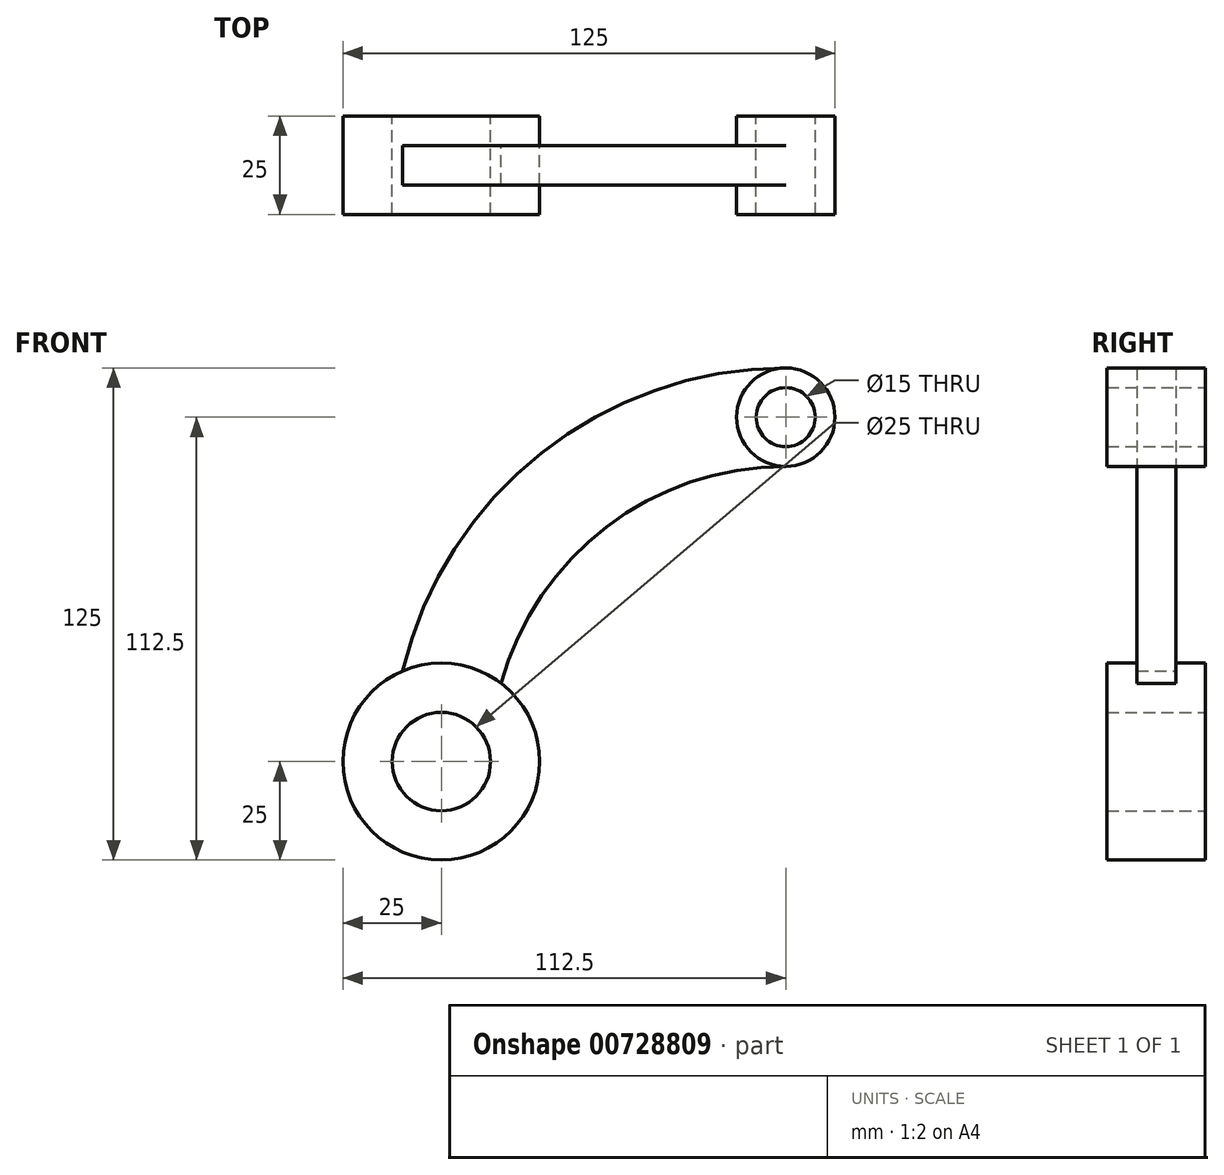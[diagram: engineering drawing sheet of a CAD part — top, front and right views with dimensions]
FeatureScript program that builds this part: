
annotation { "Feature Type Name" : "Feature", "Feature Type Description" : "" }
export const myFeature = defineFeature(function(context is Context, id is Id, definition is map)
    precondition{}
    {
        {
            var Q0;
            Q0=qCreatedBy(makeId("Front.planeOp"),FACE);
            var sketch = newSketch(context, id + "F0", { "sketchPlane" : qUnion([Q0])});
            skArc(sketch, "E0", {"start": v(0, 75) * mm, "mid": v(-45.47, 59.64) * mm, "end": v(-72.32, 19.86) * mm});
            skArc(sketch, "E1", {"start": v(0, 100) * mm, "mid": v(-62.05, 78.42) * mm, "end": v(-97.32, 22.99) * mm});
            skCircle(sketch, "E2", {"center": v(0, 87.5) * mm, "radius": 12.5 * mm});
            skCircle(sketch, "E3", {"center": v(0, 87.5) * mm, "radius": 7.5 * mm});
            skCircle(sketch, "E4", {"center": v(-87.5, 0) * mm, "radius": 25 * mm});
            skCircle(sketch, "E5", {"center": v(-87.5, 0) * mm, "radius": 12.5 * mm});
            skSolve(sketch);
        }
        {
            var Q0;
            Q0=makeQuery(id+"F0.imprint","IMPRINT",FACE,{"disambiguationData":[TD([[makeQuery(id+"F0.imprint","IMPRINT",EDGE,{"derivedFrom":sQuery(id+"F0.wireOp",EDGE,"E5")}),-1.0]])]});
            var Q1;
            Q1=makeQuery(id+"F0.imprint","IMPRINT",FACE,{"disambiguationData":[TD([[makeQuery(id+"F0.imprint","IMPRINT",EDGE,{"derivedFrom":sQuery(id+"F0.wireOp",EDGE,"E3")}),-1.0]])]});
            extrude(context, id + "F1", {"entities" : qUnion([Q0, Q1]), "depth" : 25 * mm, "offsetDistance" : 25 * mm, "symmetric" : true});
        }
        {
            var Q0;
            {var subQ0=sQuery(id+"F0.wireOp",EDGE,"E0");Q0=makeQuery(id+"F0.imprint","IMPRINT",FACE,{"disambiguationData":[TD([[makeQuery(id+"F0.imprint","IMPRINT",EDGE,{"derivedFrom":subQ0}),-1.0]])]});}
            extrude(context, id + "F2", {"entities" : qUnion([Q0]), "operationType" : NewBodyOperationType.ADD, "depth" : 10 * mm, "offsetDistance" : 25 * mm, "symmetric" : true});
        }
    });
